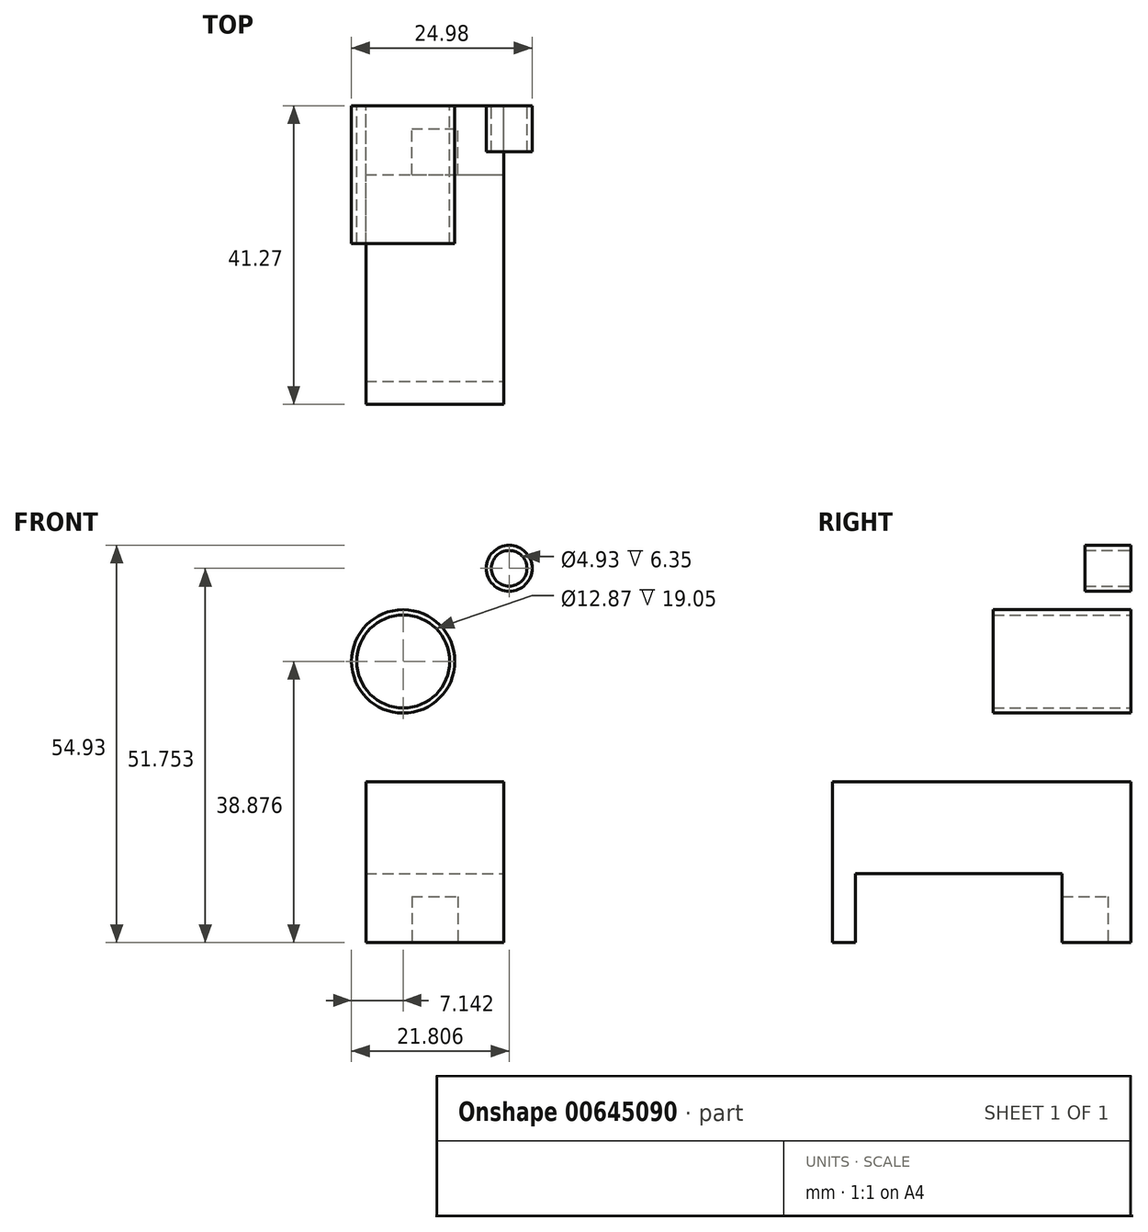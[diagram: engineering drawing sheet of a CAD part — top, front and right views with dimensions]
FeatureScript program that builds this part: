
annotation { "Feature Type Name" : "Feature", "Feature Type Description" : "" }
export const myFeature = defineFeature(function(context is Context, id is Id, definition is map)
    precondition{}
    {
        {
            var Q0;
            Q0=qCreatedBy(makeId("Front.planeOp"),FACE);
            var sketch = newSketch(context, id + "F0", { "sketchPlane" : qUnion([Q0])});
            skCircle(sketch, "E0", {"center": v(-58.64, 47.78) * mm, "radius": 7.14 * mm});
            skCircle(sketch, "E1", {"center": v(-58.64, 47.78) * mm, "radius": 6.43 * mm});
            skSolve(sketch);
        }
        {
            var Q0;
            Q0=makeQuery(id+"F0.imprint","IMPRINT",FACE,{"disambiguationData":[TD([[makeQuery(id+"F0.imprint","IMPRINT",EDGE,{"derivedFrom":sQuery(id+"F0.wireOp",EDGE,"E0")}),1.0]])]});
            extrude(context, id + "F1", {"entities" : qUnion([Q0]), "depth" : 19.05 * mm, "offsetDistance" : 25.4 * mm});
        }
        {
            var Q0;
            Q0=qCreatedBy(makeId("Front.planeOp"),FACE);
            var sketch = newSketch(context, id + "F2", { "sketchPlane" : qUnion([Q0])});
            skCircle(sketch, "E2", {"center": v(-43.97, 60.65) * mm, "radius": 3.18 * mm});
            skCircle(sketch, "E3", {"center": v(-43.97, 60.65) * mm, "radius": 2.46 * mm});
            skSolve(sketch);
        }
        {
            var Q0;
            Q0=makeQuery(id+"F2.imprint","IMPRINT",FACE,{"disambiguationData":[TD([[makeQuery(id+"F2.imprint","IMPRINT",EDGE,{"derivedFrom":sQuery(id+"F2.wireOp",EDGE,"E2")}),1.0]])]});
            extrude(context, id + "F3", {"entities" : qUnion([Q0]), "depth" : 6.35 * mm, "offsetDistance" : 25.4 * mm});
        }
        {
            var Q0;
            Q0=qCreatedBy(makeId("Front.planeOp"),FACE);
            var sketch = newSketch(context, id + "F4", { "sketchPlane" : qUnion([Q0])});
            skLineSegment(sketch, "E4.bottom", {"start": v(-63.79, 31.12) * mm, "end": v(-44.74, 31.12) * mm});
            skLineSegment(sketch, "E4.top", {"start": v(-63.79, 8.9) * mm, "end": v(-44.74, 8.9) * mm});
            skLineSegment(sketch, "E4.left", {"start": v(-63.79, 31.12) * mm, "end": v(-63.79, 8.9) * mm});
            skLineSegment(sketch, "E4.right", {"start": v(-44.74, 31.12) * mm, "end": v(-44.74, 8.9) * mm});
            skSolve(sketch);
        }
        {
            var Q0;
            Q0 = qSketchRegion(id + "F4", true);
            extrude(context, id + "F5", {"entities" : qUnion([Q0]), "depth" : 41.27 * mm, "offsetDistance" : 25.4 * mm});
        }
        {
            var Q0;
            Q0=makeQuery(id+"F5.opExtrude","SWEPT_FACE",FACE,{"disambiguationData":[OSD([sQuery(id+"F4.wireOp",EDGE,"E4.top")])]});
            var sketch = newSketch(context, id + "F6", { "sketchPlane" : qUnion([Q0])});
            skLineSegment(sketch, "E5.bottom", {"start": v(-63.79, 38.1) * mm, "end": v(-44.74, 38.1) * mm});
            skLineSegment(sketch, "E5.top", {"start": v(-63.79, 9.53) * mm, "end": v(-44.74, 9.53) * mm});
            skLineSegment(sketch, "E5.left", {"start": v(-63.79, 38.1) * mm, "end": v(-63.79, 9.53) * mm});
            skLineSegment(sketch, "E5.right", {"start": v(-44.74, 38.1) * mm, "end": v(-44.74, 9.53) * mm});
            skSolve(sketch);
        }
        {
            var Q0;
            Q0=makeQuery(id+"F6.imprint","IMPRINT",FACE,{"disambiguationData":[TD([[makeQuery(id+"F6.imprint","IMPRINT",EDGE,{"derivedFrom":sQuery(id+"F6.wireOp",EDGE,"E5.bottom")}),-1.0]])]});
            extrude(context, id + "F7", {"entities" : qUnion([Q0]), "operationType" : NewBodyOperationType.REMOVE, "oppositeDirection" : true, "depth" : 9.52 * mm, "offsetDistance" : 25.4 * mm});
        }
        {
            var Q0;
            {var subQ2=sQuery(id+"F4.wireOp",EDGE,"E4.top");Q0=makeQuery(id+"F7.boolean.opBoolean","SPLIT",FACE,{"disambiguationData":[TD([makeQuery(id+"F7.opExtrude","SWEPT_FACE",FACE,{"disambiguationData":[OSD([sQuery(id+"F6.wireOp",EDGE,"E5.top")])]})])],"derivedFrom":makeQuery(id+"F5.opExtrude","SWEPT_FACE",FACE,{"disambiguationData":[OSD([subQ2])]})});}
            var sketch = newSketch(context, id + "F8", { "sketchPlane" : qUnion([Q0])});
            skLineSegment(sketch, "E6.bottom", {"start": v(-57.44, 9.53) * mm, "end": v(-51.09, 9.53) * mm});
            skLineSegment(sketch, "E6.top", {"start": v(-57.44, 3.18) * mm, "end": v(-51.09, 3.18) * mm});
            skLineSegment(sketch, "E6.left", {"start": v(-57.44, 9.53) * mm, "end": v(-57.44, 3.18) * mm});
            skLineSegment(sketch, "E6.right", {"start": v(-51.09, 9.53) * mm, "end": v(-51.09, 3.18) * mm});
            skSolve(sketch);
        }
        {
            var Q0;
            Q0=makeQuery(id+"F8.imprint","IMPRINT",FACE,{"disambiguationData":[TD([[makeQuery(id+"F8.imprint","IMPRINT",EDGE,{"derivedFrom":sQuery(id+"F8.wireOp",EDGE,"E6.bottom")}),-1.0]])]});
            extrude(context, id + "F9", {"entities" : qUnion([Q0]), "operationType" : NewBodyOperationType.REMOVE, "oppositeDirection" : true, "depth" : 6.35 * mm, "offsetDistance" : 25.4 * mm});
        }
    });
